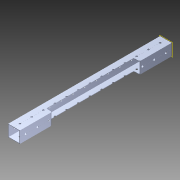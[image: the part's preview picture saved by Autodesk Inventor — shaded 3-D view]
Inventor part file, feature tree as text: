
AUTODESK INVENTOR PART (.ipt)
format: ipt  version: 2014 (Build 180170000, 170)  size: 1,245,184 bytes
history: native  units: in
note: dims shown in document units (in); Inventor stores cm internally (conversion verified against a paired STEP export)
features: extrude x2, sketch x2, pattern_circular x1, other x1, plane x1, imported_body x1
ambient origin geometry x8: Origin, YZ Plane, XZ Plane, XY Plane, X Axis, Y Axis, Z Axis, Center Point
bodies: Body1 (feature_tree)
feature tree (8):
  pattern_circular  "CirPattern2"
  other  "217-3426-STEP1"
  plane  "Work Plane1"
  extrude  "Extrusion1"  Depth=3937.0079in TaperAngle=0.0deg
  extrude  "Extrusion3"  Depth=0.125in
  imported_body  "Base1"
  sketch  "Sketch1"  dims[d0=-13.0in d1=3937.0079in d2=0.0in]
  sketch  "Sketch4"  dims[d6=7.5in d9=0.125in d10=0.125in d11=0.5in d12=2.75in d13=3.937in d14=0.0in]
